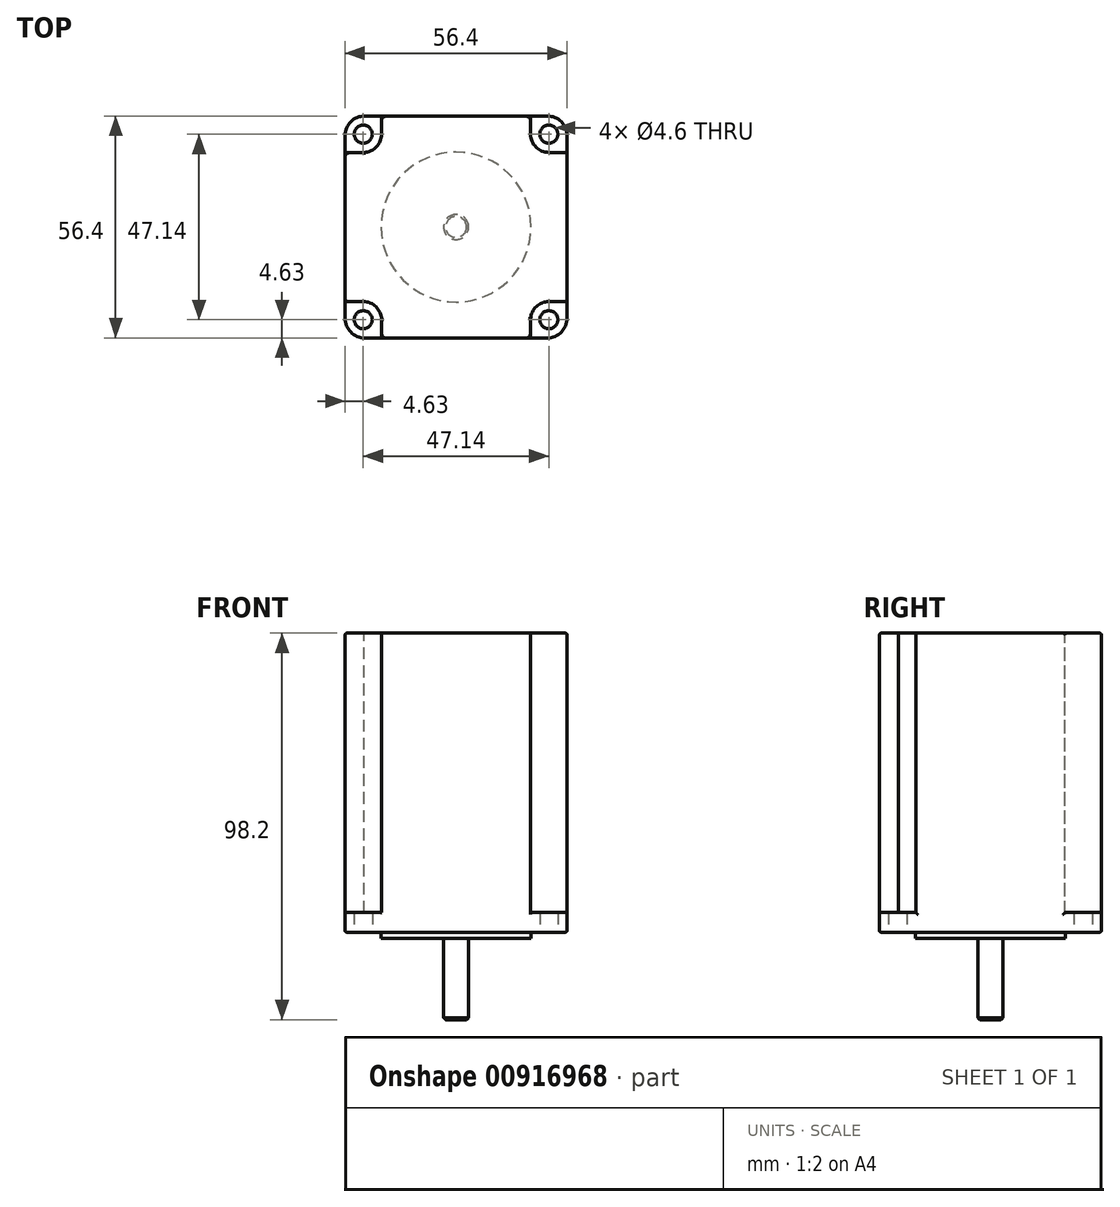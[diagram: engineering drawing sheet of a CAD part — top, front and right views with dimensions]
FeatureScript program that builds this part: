
annotation { "Feature Type Name" : "Feature", "Feature Type Description" : "" }
export const myFeature = defineFeature(function(context is Context, id is Id, definition is map)
    precondition{}
    {
        {
            var Q0;
            Q0=qCreatedBy(makeId("Top.planeOp"),FACE);
            var sketch = newSketch(context, id + "F0", { "sketchPlane" : qUnion([Q0])});
            skLineSegment(sketch, "E0.bottom", {"start": v(0, 0) * mm, "end": v(56.4, 0) * mm});
            skLineSegment(sketch, "E0.top", {"start": v(0, 56.4) * mm, "end": v(56.4, 56.4) * mm});
            skLineSegment(sketch, "E0.left", {"start": v(0, 0) * mm, "end": v(0, 56.4) * mm});
            skLineSegment(sketch, "E0.right", {"start": v(56.4, 0) * mm, "end": v(56.4, 56.4) * mm});
            skSolve(sketch);
        }
        {
            var Q0;
            Q0=makeQuery(id+"F0.imprint","IMPRINT",FACE,{"disambiguationData":[TD([[makeQuery(id+"F0.imprint","IMPRINT",EDGE,{"derivedFrom":sQuery(id+"F0.wireOp",EDGE,"E0.bottom")}),1.0]])]});
            extrude(context, id + "F1", {"entities" : qUnion([Q0]), "depth" : 76 * mm, "offsetDistance" : 25 * mm});
        }
        {
            var Q0;
            Q0=makeQuery(id+"F1.opExtrude","CAP_FACE",FACE,{"disambiguationData":[OSD([sQuery(id+"F0.wireOp",EDGE,"E0.bottom"),sQuery(id+"F0.wireOp",EDGE,"E0.top"),sQuery(id+"F0.wireOp",EDGE,"E0.left"),sQuery(id+"F0.wireOp",EDGE,"E0.right")])],"isStart":true});
            var sketch = newSketch(context, id + "F2", { "sketchPlane" : qUnion([Q0])});
            skLineSegment(sketch, "E1.bottom", {"start": v(4.63, -4.63) * mm, "end": v(51.77, -4.63) * mm, "construction": true});
            skLineSegment(sketch, "E1.top", {"start": v(4.63, -51.77) * mm, "end": v(51.77, -51.77) * mm, "construction": true});
            skLineSegment(sketch, "E1.left", {"start": v(4.63, -4.63) * mm, "end": v(4.63, -51.77) * mm, "construction": true});
            skLineSegment(sketch, "E1.right", {"start": v(51.77, -4.63) * mm, "end": v(51.77, -51.77) * mm, "construction": true});
            skCircle(sketch, "E2", {"center": v(4.63, -4.63) * mm, "radius": 2.3 * mm});
            skCircle(sketch, "E3", {"center": v(51.77, -4.63) * mm, "radius": 2.3 * mm});
            skCircle(sketch, "E4", {"center": v(4.63, -51.77) * mm, "radius": 2.3 * mm});
            skCircle(sketch, "E5", {"center": v(51.77, -51.77) * mm, "radius": 2.3 * mm});
            skSolve(sketch);
        }
        {
            var Q0;
            Q0=makeQuery(id+"F2.imprint","IMPRINT",FACE,{"disambiguationData":[TD([[makeQuery(id+"F2.imprint","IMPRINT",EDGE,{"derivedFrom":sQuery(id+"F2.wireOp",EDGE,"E2")}),1.0]])]});
            var Q1;
            Q1=makeQuery(id+"F2.imprint","IMPRINT",FACE,{"disambiguationData":[TD([[makeQuery(id+"F2.imprint","IMPRINT",EDGE,{"derivedFrom":sQuery(id+"F2.wireOp",EDGE,"E3")}),1.0]])]});
            var Q2;
            Q2=makeQuery(id+"F2.imprint","IMPRINT",FACE,{"disambiguationData":[TD([[makeQuery(id+"F2.imprint","IMPRINT",EDGE,{"derivedFrom":sQuery(id+"F2.wireOp",EDGE,"E5")}),1.0]])]});
            var Q3;
            Q3=makeQuery(id+"F2.imprint","IMPRINT",FACE,{"disambiguationData":[TD([[makeQuery(id+"F2.imprint","IMPRINT",EDGE,{"derivedFrom":sQuery(id+"F2.wireOp",EDGE,"E4")}),1.0]])]});
            extrude(context, id + "F3", {"entities" : qUnion([Q0, Q1, Q2, Q3]), "operationType" : NewBodyOperationType.REMOVE, "endBound" : BoundingType.THROUGH_ALL, "oppositeDirection" : true, "depth" : 25 * mm, "offsetDistance" : 25 * mm});
        }
        {
            var Q0;
            Q0=makeQuery(id+"F1.opExtrude","CAP_FACE",FACE,{"disambiguationData":[OSD([sQuery(id+"F0.wireOp",EDGE,"E0.bottom"),sQuery(id+"F0.wireOp",EDGE,"E0.top"),sQuery(id+"F0.wireOp",EDGE,"E0.left"),sQuery(id+"F0.wireOp",EDGE,"E0.right")])],"isStart":false});
            var sketch = newSketch(context, id + "F4", { "sketchPlane" : qUnion([Q0])});
            skArc(sketch, "E6", {"start": v(4.44, 47.14) * mm, "mid": v(7.85, 48.44) * mm, "end": v(9.26, 51.8) * mm});
            skArc(sketch, "E7", {"start": v(47.14, 51.75) * mm, "mid": v(48.5, 48.49) * mm, "end": v(51.77, 47.14) * mm});
            skArc(sketch, "E8", {"start": v(9.26, 4.54) * mm, "mid": v(7.94, 7.87) * mm, "end": v(4.63, 9.26) * mm});
            skLineSegment(sketch, "E9", {"start": v(0, 47.14) * mm, "end": v(4.82, 47.14) * mm});
            skLineSegment(sketch, "E10.trimOffspring", {"start": v(51.77, 47.14) * mm, "end": v(56.4, 47.14) * mm});
            skLineSegment(sketch, "E11", {"start": v(47.14, 51.75) * mm, "end": v(47.12, 56.4) * mm});
            skLineSegment(sketch, "E12", {"start": v(9.26, 51.8) * mm, "end": v(9.26, 56.4) * mm});
            skLineSegment(sketch, "E13", {"start": v(47.12, 56.4) * mm, "end": v(56.4, 56.4) * mm});
            skLineSegment(sketch, "E14", {"start": v(56.4, 56.4) * mm, "end": v(56.4, 47.14) * mm});
            skLineSegment(sketch, "E15", {"start": v(9.26, 56.4) * mm, "end": v(0, 56.4) * mm});
            skLineSegment(sketch, "E16", {"start": v(0, 56.4) * mm, "end": v(0, 47.14) * mm});
            skLineSegment(sketch, "E17", {"start": v(4.63, 9.26) * mm, "end": v(0, 9.26) * mm});
            skLineSegment(sketch, "E18", {"start": v(9.26, 4.72) * mm, "end": v(9.26, 0) * mm});
            skLineSegment(sketch, "E19", {"start": v(0, 0) * mm, "end": v(9.26, 0) * mm});
            skLineSegment(sketch, "E20", {"start": v(0, 9.26) * mm, "end": v(0, 0) * mm});
            skLineSegment(sketch, "E21", {"start": v(51.77, 9.26) * mm, "end": v(56.4, 9.26) * mm});
            skLineSegment(sketch, "E22", {"start": v(56.4, 9.26) * mm, "end": v(56.4, 0) * mm});
            skLineSegment(sketch, "E23", {"start": v(47.15, 4.88) * mm, "end": v(47.15, 0) * mm});
            skLineSegment(sketch, "E24", {"start": v(47.15, 0) * mm, "end": v(56.4, 0) * mm});
            skArc(sketch, "E25.trimOffspring", {"start": v(51.77, 9.26) * mm, "mid": v(48.4, 7.81) * mm, "end": v(47.15, 4.38) * mm});
            skSolve(sketch);
        }
        {
            var Q0;
            {var subQ0=sQuery(id+"F4.wireOp",EDGE,"E12");Q0=makeQuery(id+"F4.imprint","IMPRINT",FACE,{"disambiguationData":[TD([[makeQuery(id+"F4.imprint","IMPRINT",EDGE,{"derivedFrom":subQ0}),1.0]])]});}
            var Q1;
            {var subQ6=sQuery(id+"F4.wireOp",EDGE,"E17");Q1=makeQuery(id+"F4.imprint","IMPRINT",FACE,{"disambiguationData":[TD([[makeQuery(id+"F4.imprint","IMPRINT",EDGE,{"derivedFrom":subQ6}),1.0]])]});}
            var Q2;
            {var subQ6=sQuery(id+"F4.wireOp",EDGE,"E21");Q2=makeQuery(id+"F4.imprint","IMPRINT",FACE,{"disambiguationData":[TD([[makeQuery(id+"F4.imprint","IMPRINT",EDGE,{"derivedFrom":subQ6}),-1.0]])]});}
            var Q3;
            Q3=makeQuery(id+"F4.imprint","IMPRINT",FACE,{"disambiguationData":[TD([[makeQuery(id+"F4.imprint","IMPRINT",EDGE,{"derivedFrom":sQuery(id+"F4.wireOp",EDGE,"E7")}),1.0]])]});
            extrude(context, id + "F5", {"entities" : qUnion([Q0, Q1, Q2, Q3]), "operationType" : NewBodyOperationType.REMOVE, "oppositeDirection" : true, "depth" : 71 * mm, "offsetDistance" : 25 * mm});
        }
        {
            var Q0;
            Q0=makeQuery(id+"F1.opExtrude","SWEPT_EDGE",EDGE,{"disambiguationData":[OSD([sQuery(id+"F0.wireOp",EDGE,"E0.top"),sQuery(id+"F0.wireOp",EDGE,"E0.right")])]});
            var Q1;
            Q1=makeQuery(id+"F1.opExtrude","SWEPT_EDGE",EDGE,{"disambiguationData":[OSD([sQuery(id+"F0.wireOp",EDGE,"E0.top"),sQuery(id+"F0.wireOp",EDGE,"E0.left")])]});
            var Q2;
            Q2=makeQuery(id+"F1.opExtrude","SWEPT_EDGE",EDGE,{"disambiguationData":[OSD([sQuery(id+"F0.wireOp",EDGE,"E0.bottom"),sQuery(id+"F0.wireOp",EDGE,"E0.left")])]});
            var Q3;
            Q3=makeQuery(id+"F1.opExtrude","SWEPT_EDGE",EDGE,{"disambiguationData":[OSD([sQuery(id+"F0.wireOp",EDGE,"E0.bottom"),sQuery(id+"F0.wireOp",EDGE,"E0.right")])]});
            fillet(context, id + "F6", {"entities" : qUnion([Q0, Q1, Q2, Q3]), "radius" : 5 * mm, "tangentPropagation" : true, "allowEdgeOverflow" : false});
        }
        {
            var Q0;
            Q0=makeQuery(id+"F1.opExtrude","CAP_FACE",FACE,{"disambiguationData":[OSD([sQuery(id+"F0.wireOp",EDGE,"E0.bottom"),sQuery(id+"F0.wireOp",EDGE,"E0.top"),sQuery(id+"F0.wireOp",EDGE,"E0.left"),sQuery(id+"F0.wireOp",EDGE,"E0.right")])],"isStart":true});
            var sketch = newSketch(context, id + "F7", { "sketchPlane" : qUnion([Q0])});
            skCircle(sketch, "E26", {"center": v(28.2, -28.2) * mm, "radius": 19.05 * mm});
            skPoint(sketch, "E26.centerSnap0", {"position": v(56.4, -28.2) * mm});
            skPoint(sketch, "E26.centerSnap1", {"position": v(28.2, 0) * mm});
            skSolve(sketch);
        }
        {
            var Q0;
            Q0=makeQuery(id+"F7.imprint","IMPRINT",FACE,{"disambiguationData":[TD([[makeQuery(id+"F7.imprint","IMPRINT",EDGE,{"derivedFrom":sQuery(id+"F7.wireOp",EDGE,"E26")}),1.0]])]});
            extrude(context, id + "F8", {"entities" : qUnion([Q0]), "operationType" : NewBodyOperationType.ADD, "depth" : 1.6 * mm, "offsetDistance" : 25 * mm});
        }
        {
            var Q0;
            Q0=makeQuery(id+"F8.opExtrude","CAP_FACE",FACE,{"disambiguationData":[OSD([sQuery(id+"F7.wireOp",EDGE,"E26")])],"isStart":false});
            var sketch = newSketch(context, id + "F9", { "sketchPlane" : qUnion([Q0])});
            skCircle(sketch, "E27", {"center": v(28.2, -28.2) * mm, "radius": 3.17 * mm});
            skSolve(sketch);
        }
        {
            var Q0;
            Q0=makeQuery(id+"F9.imprint","IMPRINT",FACE,{"disambiguationData":[TD([[makeQuery(id+"F9.imprint","IMPRINT",EDGE,{"derivedFrom":sQuery(id+"F9.wireOp",EDGE,"E27")}),1.0]])]});
            extrude(context, id + "F10", {"entities" : qUnion([Q0]), "operationType" : NewBodyOperationType.ADD, "depth" : 20.6 * mm, "offsetDistance" : 25 * mm});
        }
        {
            var Q0;
            Q0=makeQuery(id+"F10.opExtrude","CAP_EDGE",EDGE,{"disambiguationData":[OSD([sQuery(id+"F9.wireOp",EDGE,"E27")])],"isStart":false});
            chamfer(context, id + "F11", {"entities" : qUnion([Q0]), "width" : .5 * mm, "tangentPropagation" : true});
        }
        {
            var Q0;
            Q0=makeQuery(id+"F1.opExtrude","CAP_EDGE",EDGE,{"disambiguationData":[OSD([sQuery(id+"F0.wireOp",EDGE,"E0.left")])],"isStart":true});
            var Q1;
            Q1=makeQuery(id+"F1.opExtrude","CAP_FACE",FACE,{"disambiguationData":[OSD([sQuery(id+"F0.wireOp",EDGE,"E0.bottom"),sQuery(id+"F0.wireOp",EDGE,"E0.top"),sQuery(id+"F0.wireOp",EDGE,"E0.left"),sQuery(id+"F0.wireOp",EDGE,"E0.right")])],"isStart":false});
            var Q2;
            Q2=makeQuery(id+"F5.boolean.opBoolean","COPY",EDGE,{"derivedFrom":makeQuery(id+"F5.opExtrude","SWEPT_EDGE",EDGE,{"disambiguationData":[OSD([sQuery(id+"F0.wireOp",EDGE,"E0.bottom"),sQuery(id+"F4.wireOp",EDGE,"E18"),sQuery(id+"F4.wireOp",EDGE,"E19")])]})});
            var Q3;
            Q3=makeQuery(id+"F5.boolean.opBoolean","COPY",EDGE,{"derivedFrom":makeQuery(id+"F5.opExtrude","SWEPT_EDGE",EDGE,{"disambiguationData":[OSD([sQuery(id+"F0.wireOp",EDGE,"E0.bottom"),sQuery(id+"F4.wireOp",EDGE,"E23"),sQuery(id+"F4.wireOp",EDGE,"E24")])]})});
            var Q4;
            Q4=makeQuery(id+"F5.boolean.opBoolean","COPY",EDGE,{"derivedFrom":makeQuery(id+"F5.opExtrude","SWEPT_EDGE",EDGE,{"disambiguationData":[OSD([sQuery(id+"F0.wireOp",EDGE,"E0.right"),sQuery(id+"F4.wireOp",EDGE,"E21"),sQuery(id+"F4.wireOp",EDGE,"E22")])]})});
            var Q5;
            Q5=makeQuery(id+"F5.boolean.opBoolean","COPY",EDGE,{"derivedFrom":makeQuery(id+"F5.opExtrude","SWEPT_EDGE",EDGE,{"disambiguationData":[OSD([sQuery(id+"F0.wireOp",EDGE,"E0.left"),sQuery(id+"F4.wireOp",EDGE,"E17"),sQuery(id+"F4.wireOp",EDGE,"E20")])]})});
            var Q6;
            Q6=makeQuery(id+"F5.boolean.opBoolean","COPY",EDGE,{"derivedFrom":makeQuery(id+"F5.opExtrude","SWEPT_EDGE",EDGE,{"disambiguationData":[OSD([sQuery(id+"F0.wireOp",EDGE,"E0.left"),sQuery(id+"F4.wireOp",EDGE,"E9"),sQuery(id+"F4.wireOp",EDGE,"E16")])]})});
            var Q7;
            Q7=makeQuery(id+"F5.boolean.opBoolean","COPY",EDGE,{"derivedFrom":makeQuery(id+"F5.opExtrude","SWEPT_EDGE",EDGE,{"disambiguationData":[OSD([sQuery(id+"F0.wireOp",EDGE,"E0.top"),sQuery(id+"F4.wireOp",EDGE,"E12"),sQuery(id+"F4.wireOp",EDGE,"E15")])]})});
            var Q8;
            Q8=makeQuery(id+"F5.boolean.opBoolean","COPY",EDGE,{"derivedFrom":makeQuery(id+"F5.opExtrude","SWEPT_EDGE",EDGE,{"disambiguationData":[OSD([sQuery(id+"F0.wireOp",EDGE,"E0.top"),sQuery(id+"F4.wireOp",EDGE,"E11"),sQuery(id+"F4.wireOp",EDGE,"E13")])]})});
            var Q9;
            Q9=makeQuery(id+"F1.opExtrude","SWEPT_FACE",FACE,{"disambiguationData":[OSD([sQuery(id+"F0.wireOp",EDGE,"E0.right")])]});
            var Q10;
            Q10=makeQuery(id+"F5.boolean.opBoolean","COPY",EDGE,{"derivedFrom":makeQuery(id+"F5.opExtrude","CAP_EDGE",EDGE,{"disambiguationData":[OSD([sQuery(id+"F4.wireOp",EDGE,"E16")])],"isStart":false})});
            var Q11;
            {var subQ0=sQuery(id+"F0.wireOp",EDGE,"E0.left");var subQ1=sQuery(id+"F0.wireOp",EDGE,"E0.top");Q11=makeQuery(id+"F6.opFillet","BLEND_EDGE",EDGE,{"blendedFrom":[makeQuery(id+"F1.opExtrude","SWEPT_EDGE",EDGE,{"disambiguationData":[OSD([subQ1,subQ0])]}),makeQuery(id+"F5.boolean.opBoolean","COPY",FACE,{"derivedFrom":makeQuery(id+"F5.opExtrude","CAP_FACE",FACE,{"disambiguationData":[OSD([sQuery(id+"F0.wireOp",EDGE,"E0.bottom"),subQ1,subQ0,sQuery(id+"F0.wireOp",EDGE,"E0.right"),sQuery(id+"F2.wireOp",EDGE,"E4"),sQuery(id+"F4.wireOp",EDGE,"E6"),sQuery(id+"F4.wireOp",EDGE,"E9"),sQuery(id+"F4.wireOp",EDGE,"E12"),sQuery(id+"F4.wireOp",EDGE,"E15"),sQuery(id+"F4.wireOp",EDGE,"E16")])],"isStart":false})})],"blendedInto":[makeQuery(id+"F5.boolean.opBoolean","COPY",FACE,{"derivedFrom":makeQuery(id+"F5.opExtrude","CAP_FACE",FACE,{"disambiguationData":[OSD([sQuery(id+"F0.wireOp",EDGE,"E0.bottom"),subQ1,subQ0,sQuery(id+"F0.wireOp",EDGE,"E0.right"),sQuery(id+"F2.wireOp",EDGE,"E4"),sQuery(id+"F4.wireOp",EDGE,"E6"),sQuery(id+"F4.wireOp",EDGE,"E9"),sQuery(id+"F4.wireOp",EDGE,"E12"),sQuery(id+"F4.wireOp",EDGE,"E15"),sQuery(id+"F4.wireOp",EDGE,"E16")])],"isStart":false})})]});}
            var Q12;
            Q12=makeQuery(id+"F5.boolean.opBoolean","COPY",EDGE,{"derivedFrom":makeQuery(id+"F5.opExtrude","CAP_EDGE",EDGE,{"disambiguationData":[OSD([sQuery(id+"F4.wireOp",EDGE,"E15")])],"isStart":false})});
            var Q13;
            Q13=makeQuery(id+"F5.boolean.opBoolean","COPY",EDGE,{"derivedFrom":makeQuery(id+"F5.opExtrude","CAP_EDGE",EDGE,{"disambiguationData":[OSD([sQuery(id+"F4.wireOp",EDGE,"E19")])],"isStart":false})});
            fillet(context, id + "F12", {"entities" : qUnion([Q0, Q1, Q2, Q3, Q4, Q5, Q6, Q7, Q8, Q9, Q10, Q11, Q12, Q13]), "radius" : .5 * mm, "tangentPropagation" : true, "allowEdgeOverflow" : false});
        }
    });
